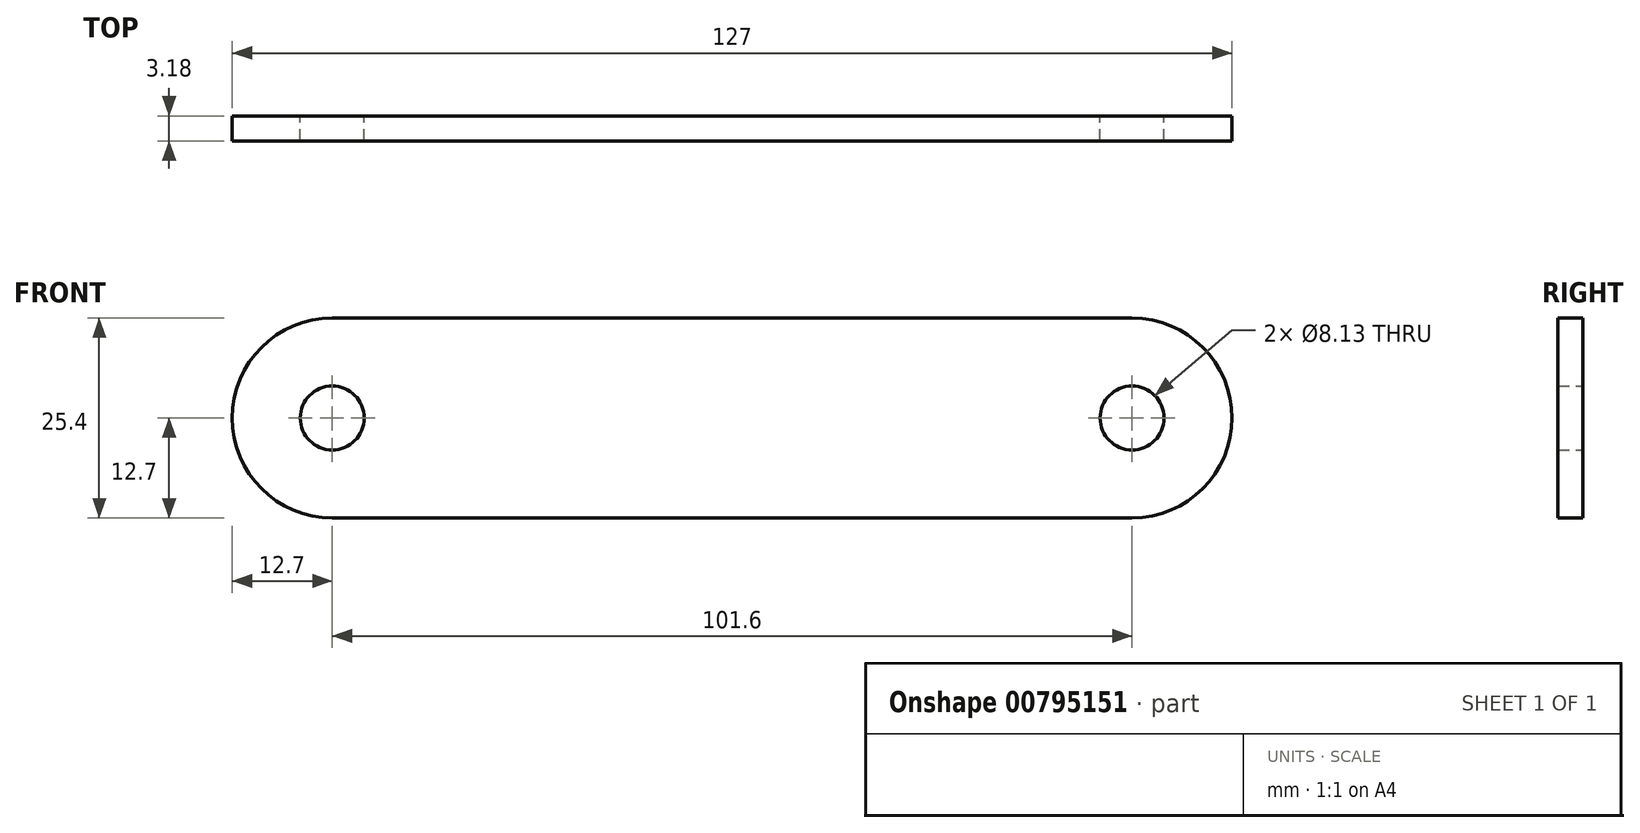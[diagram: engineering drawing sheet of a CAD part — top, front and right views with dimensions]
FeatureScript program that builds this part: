
annotation { "Feature Type Name" : "Feature", "Feature Type Description" : "" }
export const myFeature = defineFeature(function(context is Context, id is Id, definition is map)
    precondition{}
    {
        {
            var Q0;
            Q0=qCreatedBy(makeId("Front.planeOp"),FACE);
            var sketch = newSketch(context, id + "F0", { "sketchPlane" : qUnion([Q0])});
            skLineSegment(sketch, "E0.bottom", {"start": v(50.8, -12.7) * mm, "end": v(-50.8, -12.7) * mm});
            skLineSegment(sketch, "E0.top", {"start": v(50.8, 12.7) * mm, "end": v(-50.8, 12.7) * mm});
            skLineSegment(sketch, "E0.left", {"start": v(63.5, 0) * mm, "end": v(63.5, 0) * mm});
            skLineSegment(sketch, "E0.right", {"start": v(-63.5, 0) * mm, "end": v(-63.5, 0) * mm});
            skPoint(sketch, "E0.middle", {"position": v(0, 0) * mm});
            skPoint(sketch, "E1.visualSharp", {"position": v(-63.5, -12.7) * mm});
            skArc(sketch, "E1.filletArc", {"start": v(-63.5, 0) * mm, "mid": v(-59.78, -8.98) * mm, "end": v(-50.8, -12.7) * mm});
            skPoint(sketch, "E2.visualSharp", {"position": v(-63.5, 12.7) * mm});
            skArc(sketch, "E2.filletArc", {"start": v(-50.8, 12.7) * mm, "mid": v(-59.78, 8.98) * mm, "end": v(-63.5, 0) * mm});
            skPoint(sketch, "E3.visualSharp", {"position": v(63.5, 12.7) * mm});
            skArc(sketch, "E3.filletArc", {"start": v(63.5, 0) * mm, "mid": v(59.78, 8.98) * mm, "end": v(50.8, 12.7) * mm});
            skPoint(sketch, "E4.visualSharp", {"position": v(63.5, -12.7) * mm});
            skArc(sketch, "E4.filletArc", {"start": v(50.8, -12.7) * mm, "mid": v(59.78, -8.98) * mm, "end": v(63.5, 0) * mm});
            skCircle(sketch, "E5", {"center": v(50.8, 0) * mm, "radius": 4.06 * mm});
            skCircle(sketch, "E6", {"center": v(-50.8, 0) * mm, "radius": 4.06 * mm});
            skSolve(sketch);
        }
        {
            var Q0;
            Q0=makeQuery(id+"F0.imprint","IMPRINT",FACE,{"disambiguationData":[TD([[makeQuery(id+"F0.imprint","IMPRINT",EDGE,{"derivedFrom":sQuery(id+"F0.wireOp",EDGE,"E0.bottom")}),-1.0]])]});
            extrude(context, id + "F1", {"entities" : qUnion([Q0]), "depth" : 3.17 * mm, "offsetDistance" : 25.4 * mm});
        }
    });
